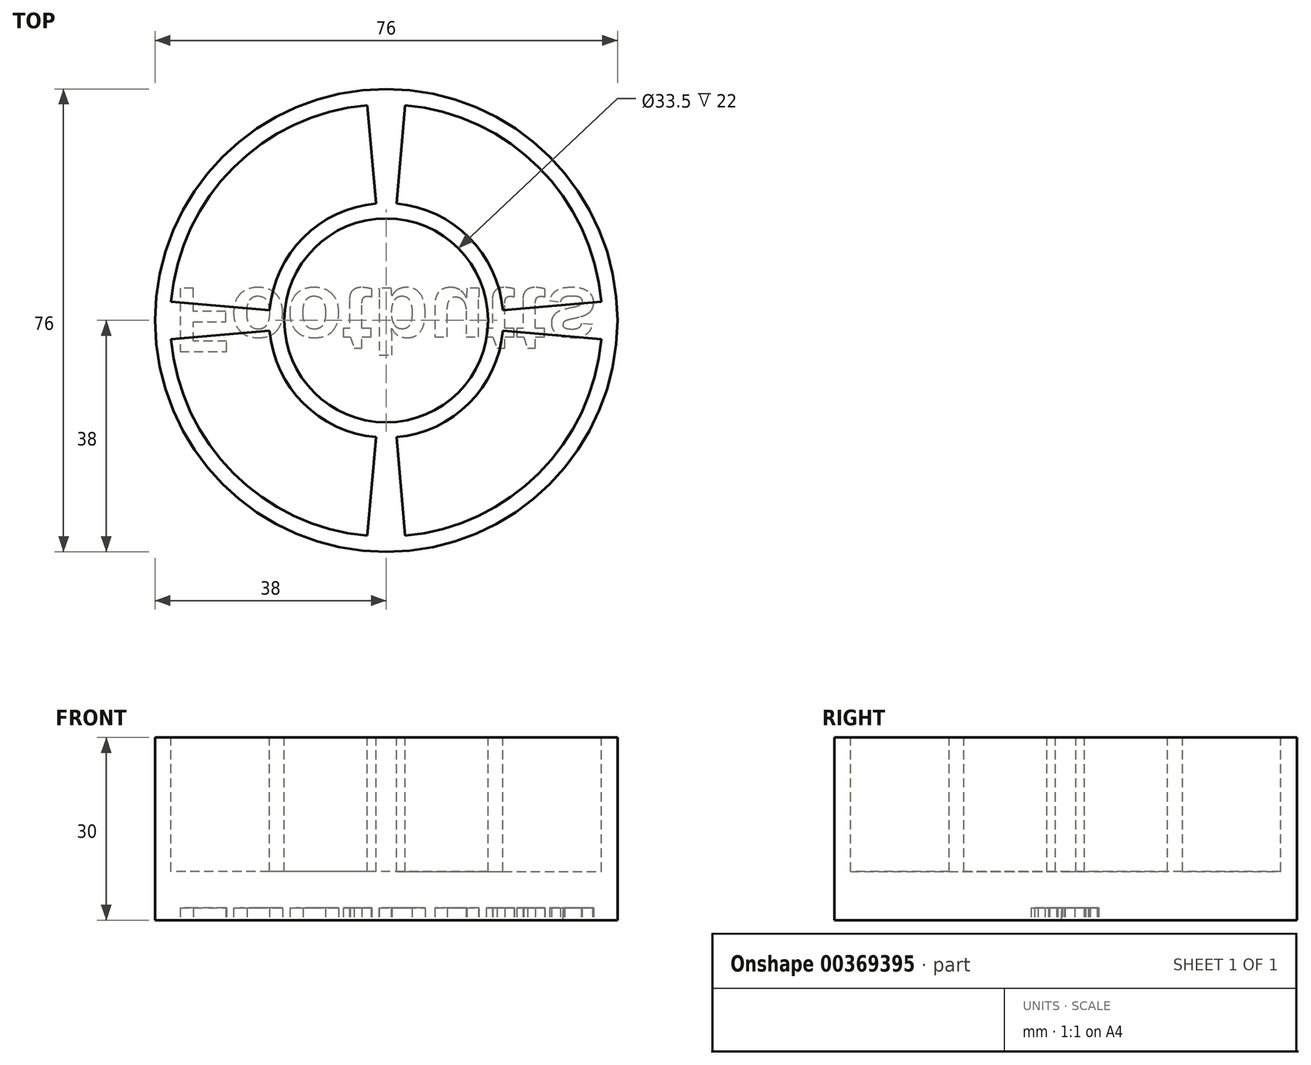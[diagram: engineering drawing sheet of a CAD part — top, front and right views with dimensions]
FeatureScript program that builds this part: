
annotation { "Feature Type Name" : "Feature", "Feature Type Description" : "" }
export const myFeature = defineFeature(function(context is Context, id is Id, definition is map)
    precondition{}
    {
        {
            var Q0;
            Q0=qCreatedBy(makeId("Top.planeOp"),FACE);
            var sketch = newSketch(context, id + "F0", { "sketchPlane" : qUnion([Q0])});
            skCircle(sketch, "E0", {"center": v(0, 0) * mm, "radius": 38 * mm});
            skSolve(sketch);
        }
        {
            var Q0;
            Q0=makeQuery(id+"F0.imprint","IMPRINT",FACE,{"disambiguationData":[TD([[makeQuery(id+"F0.imprint","IMPRINT",EDGE,{"derivedFrom":sQuery(id+"F0.wireOp",EDGE,"E0")}),1.0]])]});
            extrude(context, id + "F1", {"entities" : qUnion([Q0]), "depth" : 30 * mm});
        }
        {
            var Q0;
            Q0=makeQuery(id+"F1.opExtrude","CAP_FACE",FACE,{"disambiguationData":[OSD([sQuery(id+"F0.wireOp",EDGE,"E0")])],"isStart":false});
            var sketch = newSketch(context, id + "F2", { "sketchPlane" : qUnion([Q0])});
            skArc(sketch, "E1", {"start": v(-3.1, 35.36) * mm, "mid": v(-25.1, 25.1) * mm, "end": v(-35.36, 3.1) * mm});
            skCircle(sketch, "E2", {"center": v(0, 0) * mm, "radius": 16.75 * mm});
            skArc(sketch, "E3", {"start": v(-1.68, 19.18) * mm, "mid": v(-13.61, 13.61) * mm, "end": v(-19.18, 1.68) * mm});
            skLineSegment(sketch, "E4", {"start": v(0, -35.5) * mm, "end": v(0, 35.5) * mm, "construction": true});
            skLineSegment(sketch, "E5", {"start": v(35.5, 0) * mm, "end": v(-35.5, 0) * mm, "construction": true});
            skLineSegment(sketch, "E6", {"start": v(1.68, 19.18) * mm, "end": v(3.1, 35.36) * mm});
            skLineSegment(sketch, "E7", {"start": v(-1.68, 19.18) * mm, "end": v(-3.1, 35.36) * mm});
            skLineSegment(sketch, "E8", {"start": v(-19.18, -1.68) * mm, "end": v(-35.36, -3.1) * mm});
            skLineSegment(sketch, "E9", {"start": v(-19.18, 1.68) * mm, "end": v(-35.36, 3.1) * mm});
            skArc(sketch, "E10.trimOffspring", {"start": v(35.36, 3.1) * mm, "mid": v(25.1, 25.1) * mm, "end": v(3.1, 35.36) * mm});
            skArc(sketch, "E11.trimOffspring", {"start": v(3.1, -35.36) * mm, "mid": v(25.1, -25.1) * mm, "end": v(35.36, -3.1) * mm});
            skArc(sketch, "E12.trimOffspring", {"start": v(-35.36, -3.1) * mm, "mid": v(-25.1, -25.1) * mm, "end": v(-3.1, -35.36) * mm});
            skLineSegment(sketch, "E13.trimOffspring", {"start": v(19.18, 1.68) * mm, "end": v(35.36, 3.1) * mm});
            skLineSegment(sketch, "E14.trimOffspring", {"start": v(19.18, -1.68) * mm, "end": v(35.36, -3.1) * mm});
            skArc(sketch, "E15.trimOffspring", {"start": v(19.18, 1.68) * mm, "mid": v(13.61, 13.61) * mm, "end": v(1.68, 19.18) * mm});
            skLineSegment(sketch, "E16.trimOffspring", {"start": v(1.68, -19.18) * mm, "end": v(3.1, -35.36) * mm});
            skLineSegment(sketch, "E17.trimOffspring", {"start": v(-1.68, -19.18) * mm, "end": v(-3.1, -35.36) * mm});
            skArc(sketch, "E18.trimOffspring", {"start": v(1.68, -19.18) * mm, "mid": v(13.61, -13.61) * mm, "end": v(19.18, -1.68) * mm});
            skArc(sketch, "E19.trimOffspring", {"start": v(-19.18, -1.68) * mm, "mid": v(-13.61, -13.61) * mm, "end": v(-1.68, -19.18) * mm});
            skSolve(sketch);
        }
        {
            var Q0;
            Q0=makeQuery(id+"F2.imprint","IMPRINT",FACE,{"disambiguationData":[TD([[makeQuery(id+"F2.imprint","IMPRINT",EDGE,{"derivedFrom":sQuery(id+"F2.wireOp",EDGE,"E1")}),1.0]])]});
            var Q1;
            Q1=makeQuery(id+"F2.imprint","IMPRINT",FACE,{"disambiguationData":[TD([[makeQuery(id+"F2.imprint","IMPRINT",EDGE,{"derivedFrom":sQuery(id+"F2.wireOp",EDGE,"E6")}),-1.0]])]});
            var Q2;
            Q2=makeQuery(id+"F2.imprint","IMPRINT",FACE,{"disambiguationData":[TD([[makeQuery(id+"F2.imprint","IMPRINT",EDGE,{"derivedFrom":sQuery(id+"F2.wireOp",EDGE,"E8")}),1.0]])]});
            var Q3;
            Q3=makeQuery(id+"F2.imprint","IMPRINT",FACE,{"disambiguationData":[TD([[makeQuery(id+"F2.imprint","IMPRINT",EDGE,{"derivedFrom":sQuery(id+"F2.wireOp",EDGE,"E11.trimOffspring")}),1.0]])]});
            var Q4;
            Q4=makeQuery(id+"F2.imprint","IMPRINT",FACE,{"disambiguationData":[TD([[makeQuery(id+"F2.imprint","IMPRINT",EDGE,{"derivedFrom":sQuery(id+"F2.wireOp",EDGE,"E2")}),1.0]])]});
            extrude(context, id + "F3", {"entities" : qUnion([Q0, Q1, Q2, Q3, Q4]), "operationType" : NewBodyOperationType.REMOVE, "oppositeDirection" : true, "depth" : 22 * mm});
        }
        {
            var Q0;
            Q0=makeQuery(id+"F1.opExtrude","CAP_FACE",FACE,{"disambiguationData":[OSD([sQuery(id+"F0.wireOp",EDGE,"E0")])],"isStart":true});
            var sketch = newSketch(context, id + "F4", { "sketchPlane" : qUnion([Q0])});
            skText(sketch, "E20", { "text": "Footbutts\n", "fontName": "Arimo-Bold.ttf"});
            const initialGuessF4  = {"E20": [-0.03488, -0.00528, 1, 0, 0.01087]};
            skSetInitialGuess(sketch, initialGuessF4);
            skSolve(sketch);
        }
        {
            var Q0;
            Q0 = qSketchRegion(id + "F4", true);
            extrude(context, id + "F5", {"entities" : qUnion([Q0]), "operationType" : NewBodyOperationType.REMOVE, "oppositeDirection" : true, "depth" : 2 * mm});
        }
    });
